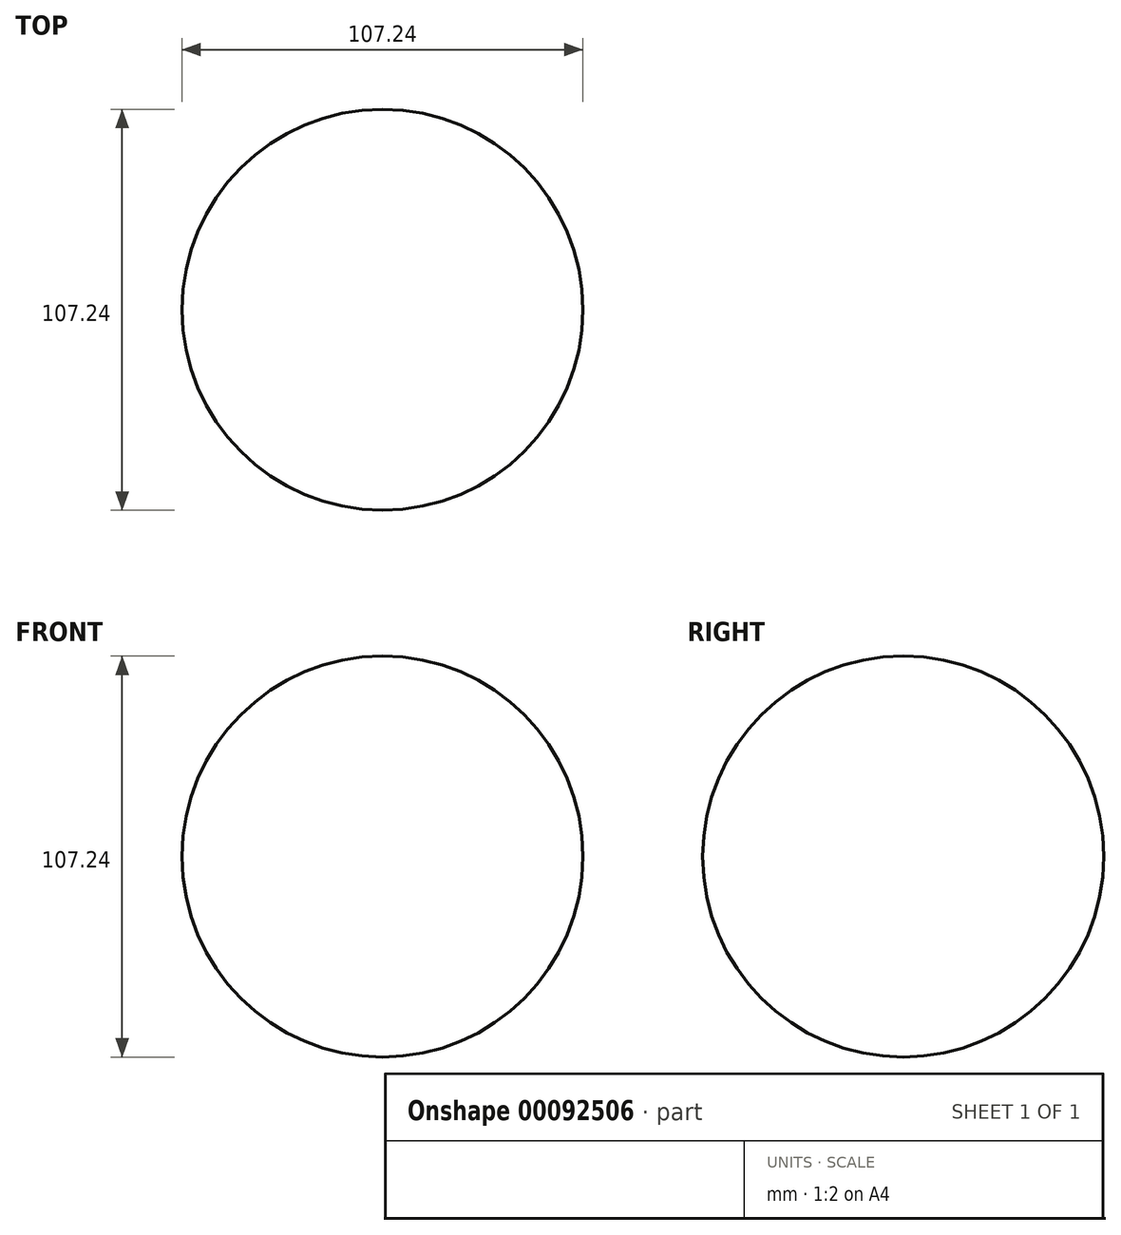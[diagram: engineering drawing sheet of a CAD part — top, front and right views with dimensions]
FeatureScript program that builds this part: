
annotation { "Feature Type Name" : "Feature", "Feature Type Description" : "" }
export const myFeature = defineFeature(function(context is Context, id is Id, definition is map)
    precondition{}
    {
        {
            var Q0;
            Q0=qCreatedBy(makeId("Top.planeOp"),FACE);
            var sketch = newSketch(context, id + "F0", { "sketchPlane" : qUnion([Q0])});
            skLineSegment(sketch, "E0", {"start": v(-53.62, 0) * mm, "end": v(53.62, 0) * mm, "construction": true});
            skArc(sketch, "E1", {"start": v(53.62, 0) * mm, "mid": v(0, 53.62) * mm, "end": v(-53.62, 0) * mm});
            skArc(sketch, "E2", {"start": v(-53.62, 0) * mm, "mid": v(0, -53.62) * mm, "end": v(53.62, 0) * mm});
            skSolve(sketch);
        }
        {
            var Q0;
            Q0=qCreatedBy(makeId("Top.planeOp"),FACE);
            var sketch = newSketch(context, id + "F1", { "sketchPlane" : qUnion([Q0])});
            skLineSegment(sketch, "E3", {"start": v(0, 0) * mm, "end": v(53.33, 0) * mm});
            skSolve(sketch);
        }
        {
            var Q0;
            Q0=sQuery(id+"F0.wireOp",EDGE,"E1");
            var Q1;
            Q1=sQuery(id+"F1.wireOp",EDGE,"E3");
            revolve(context, id + "F2", {"bodyType" : ToolBodyType.SURFACE, "surfaceEntities" : qUnion([Q0]), "axis" : qUnion([Q1]), "revolveType" : RevolveType.FULL});
        }
    });
